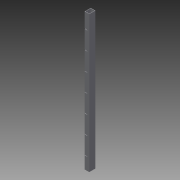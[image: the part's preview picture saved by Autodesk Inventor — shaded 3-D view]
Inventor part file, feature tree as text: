
AUTODESK INVENTOR PART (.ipt)
format: ipt  version: 2013 (Build 170138000, 138)  size: 133,632 bytes
history: native  units: in
note: dims shown in document units (in); Inventor stores cm internally (conversion verified against a paired STEP export)
features: other x4, extrude x1, sketch x1
ambient origin geometry x8: Origin, YZ Plane, XZ Plane, XY Plane, X Axis, Y Axis, Z Axis, Center Point
bodies: Solid1 (feature_tree)
feature tree (6):
  other  "Table"
  other  "squareTube1.5x2.ipt"
  extrude  "Extrusion2"  TaperAngle=0.0deg  [1 undecoded]
  other  "Solid1::squareTube1.5x2.ipt"
  other  "TaggingFeature1"
  sketch  "Sketch2"  dims[d0=1.5in d1=2.0in d2=0.125in d4=0.0in d20=2.7559in d22=6.0in d23=0.3937in d25=1.0in d27=1.0in d28=0.0in d29=0.1875in d30=4.0in d31=0.75in]
note: 1 required parameter value undecoded (feature->parameter linkage not recoverable at this tier; creation-order binding heuristic only, values carry confidence <= 0.55)
